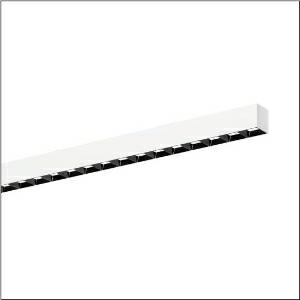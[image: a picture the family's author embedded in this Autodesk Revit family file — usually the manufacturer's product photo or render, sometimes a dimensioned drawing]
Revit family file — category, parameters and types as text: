
# Revit family: silica_21_51mx22tbt5w
name_source: partatom
category: Lighting Fixtures
units: mm (PartAtom-declared; Revit-internal decimal feet)

## family parameters
Cut with Voids When Loaded = No
Host = Face
Light Source = No
Part Type = Normal
Room Calculation Point = No
Round Connector Dimension = Use Diameter
Shared = No

## types (1)
- --- (1 x LED, 4650 lm, 40.2 W, 6500K)
    Apparent Load = 40 VA
    CIE Flux Codes = 84 100 100 100 100
    Color Rendering = 80
    Color Temperature = 6500K
    Default Elevation = 1800 mm
    Description = Silica 21, office luminaire, primary light control with darklight reflector, of PMMA, black, CAT 2 (L<= 3000cd/m²), light emission: direct distribution, primary light characteristic: symmetric, installation type: surface-mounted, LED, rated luminous flux: 4.650lm, luminous efficacy: 110lm/W, light colour: 8tw, colour temperature: 2700..6500K, control gear: DALI DT8, with terminal, 3+2-pole, max. 2.5mm², mains connection: 220..240V, AC, 50/60Hz, rated input power: 42.2W, luminaire housing, of aluminium, traffic white (RAL 9016), length: 1.504mm, width: 53mm, height: 53mm, protection rating (complete): IP20, insulation class (complete): insulation class I (protective earthing), certification: CE, permissible operating ambient temperature: 0..+35°C, standard: EN 50419, packaging unit: 1 piece
    Height = 53 mm
    Lamp = 1 x LED
    Lamp Light Flux = 4650 lm
    Lamp Power = 40.2 W
    Lamp count = 1
    Length = 1504 mm
    Luminous efficacy = 116 lm/W
    Manufacturer = Siteco
    ModVariant = No
    Model = 51MX22TBT5W
    Mounting Place = Ceiling
    Mounting Type = Surface mounted
    Number of Poles = 1
    OnlyDefault = Yes
    Power Factor = 1
    Product Name = Silica 21
    Product group = office luminaire | ceiling mounted
    ProductGroupID = 301
    Protection Class = Protection class I
    Protection Degree = IP 20
    RLX_Detail_Level = 1
    RLX_Emergency_Light_Flux = 0 lm
    RLX_Emergency_Type = 0
    RLX_Emergency_Type_DB = No
    RlxData = <blob elided: 41309 chars, md5=d9cd22f8>
    Socket = socket
    Standby Power = 0 W
    System Light Flux = 4650 lm
    System Power = 40 W
    Type Comments = individual setting
    Type Image = l_1335873.jpg
    URL = http://relux.com
    VarID = @adj_139649
    Voltage = 0 V
    Weight = 0.00 kg
    Width = 53 mm

## geometry (parser evidence)
native form markers: Blend x4, Sweep x10
no freeform markers — native parametric forms only
